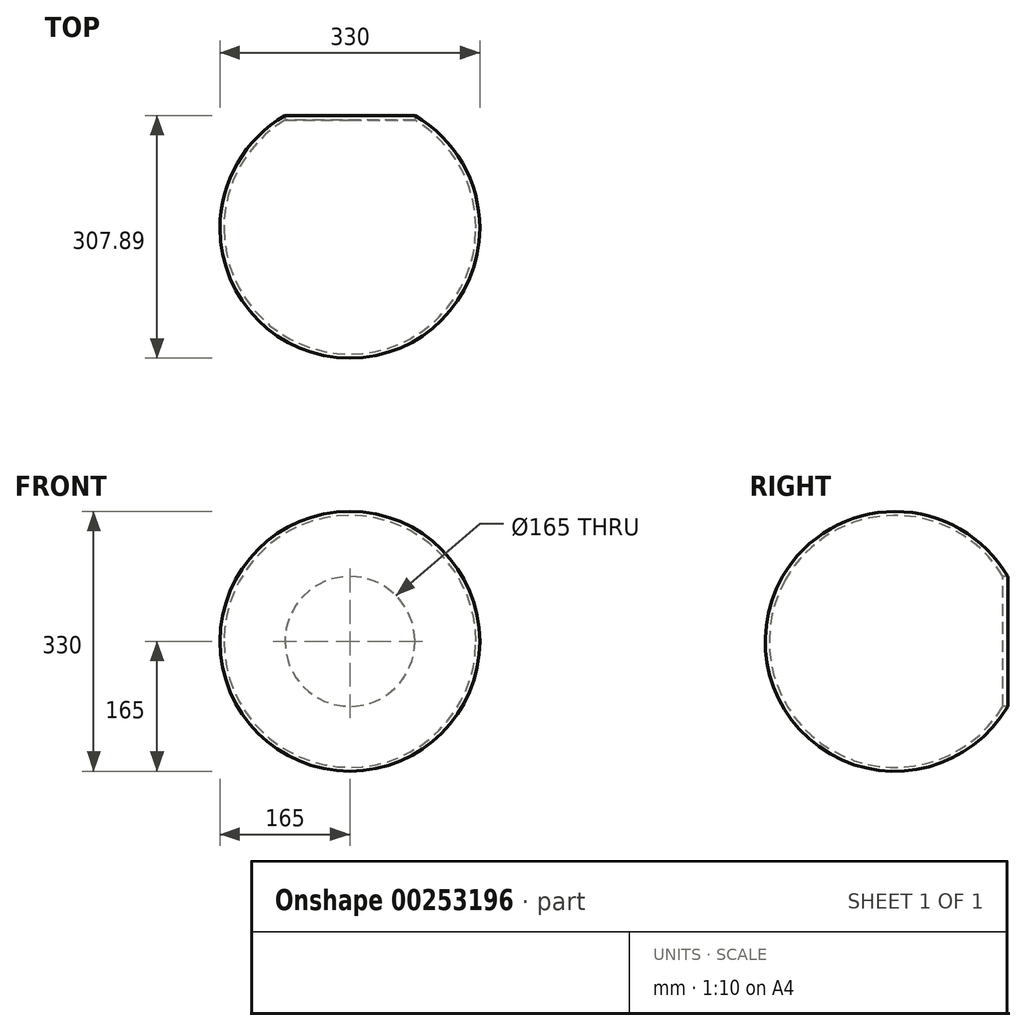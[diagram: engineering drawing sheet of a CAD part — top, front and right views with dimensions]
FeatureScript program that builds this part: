
annotation { "Feature Type Name" : "Feature", "Feature Type Description" : "" }
export const myFeature = defineFeature(function(context is Context, id is Id, definition is map)
    precondition{}
    {
        {
            var Q0;
            Q0=qCreatedBy(makeId("Front.planeOp"),FACE);
            var sketch = newSketch(context, id + "F0", { "sketchPlane" : qUnion([Q0])});
            skArc(sketch, "E0", {"start": v(160, 0) * mm, "mid": v(0, 160) * mm, "end": v(-160, 0) * mm});
            skArc(sketch, "E1", {"start": v(165, 0) * mm, "mid": v(0, 165) * mm, "end": v(-165, 0) * mm});
            skLineSegment(sketch, "E2", {"start": v(-165, 0) * mm, "end": v(-160, 0) * mm});
            skLineSegment(sketch, "E3", {"start": v(160, 0) * mm, "end": v(165, 0) * mm});
            skSolve(sketch);
        }
        {
            var Q0;
            Q0 = qSketchRegion(id + "F0", true);
            var Q1;
            Q1=sQuery(id+"F0.wireOp",EDGE,"E2");
            revolve(context, id + "F1", {"entities" : qUnion([Q0]), "axis" : qUnion([Q1]), "revolveType" : RevolveType.FULL});
        }
        {
            var Q0;
            Q0=qCreatedBy(makeId("Front.planeOp"),FACE);
            var sketch = newSketch(context, id + "F2", { "sketchPlane" : qUnion([Q0])});
            skCircle(sketch, "E4", {"center": v(0, 0) * mm, "radius": 82.5 * mm});
            skSolve(sketch);
        }
        {
            var Q0;
            Q0 = qSketchRegion(id + "F2", true);
            extrude(context, id + "F3", {"entities" : qUnion([Q0]), "operationType" : NewBodyOperationType.REMOVE, "endBound" : BoundingType.THROUGH_ALL, "oppositeDirection" : true, "depth" : 25 * mm});
        }
    });
